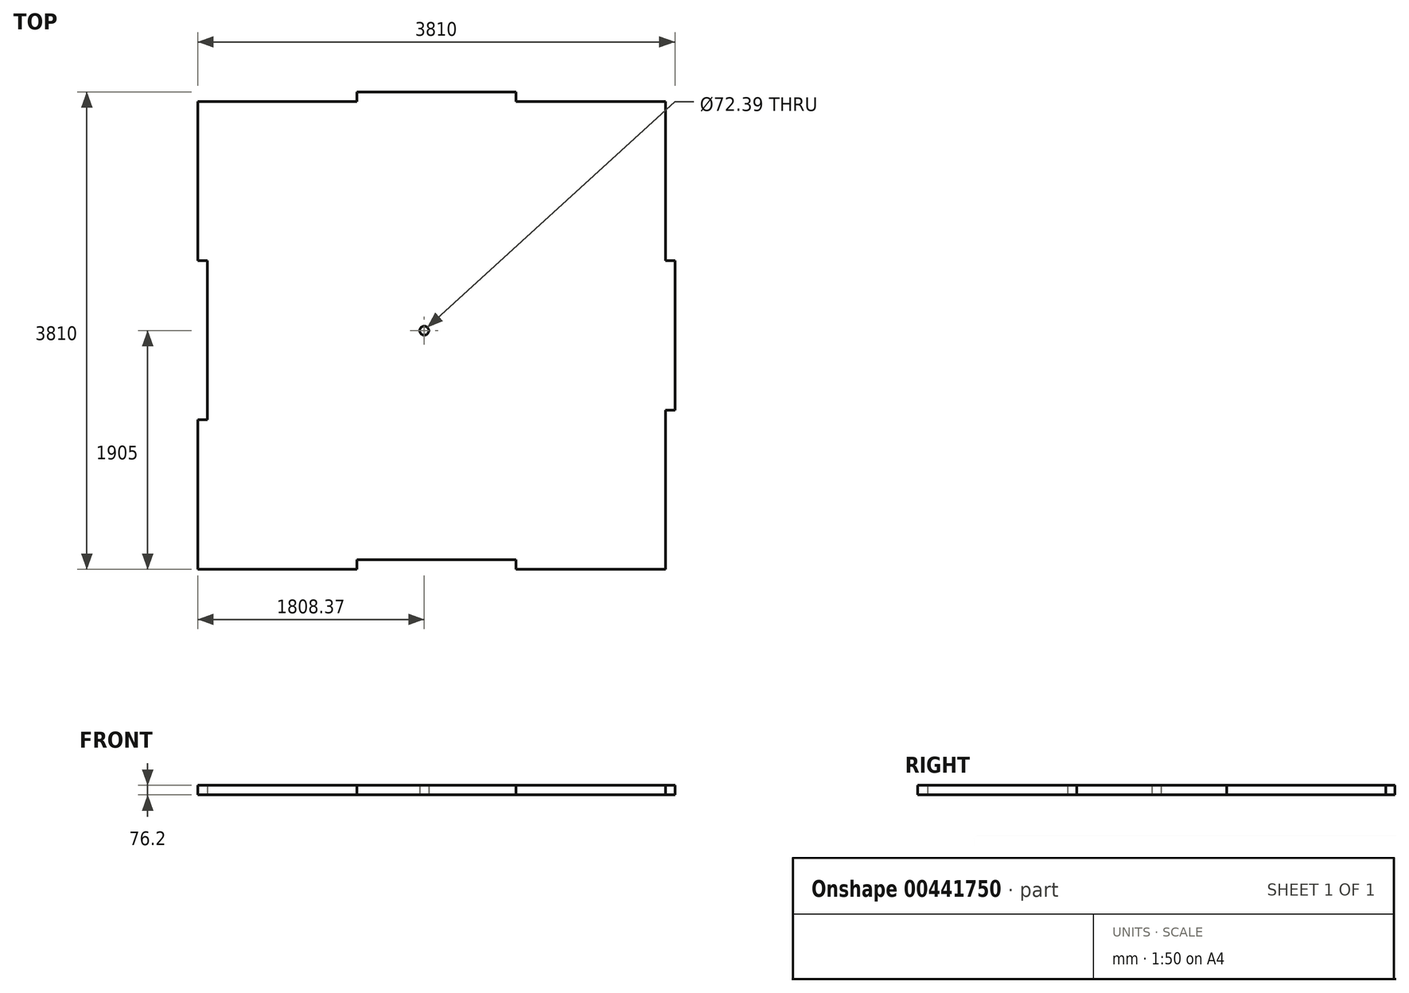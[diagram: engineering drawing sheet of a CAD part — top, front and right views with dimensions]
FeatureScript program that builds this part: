
annotation { "Feature Type Name" : "Feature", "Feature Type Description" : "" }
export const myFeature = defineFeature(function(context is Context, id is Id, definition is map)
    precondition{}
    {
        {
            var Q0;
            Q0=qCreatedBy(makeId("Top.planeOp"),FACE);
            var sketch = newSketch(context, id + "F0", { "sketchPlane" : qUnion([Q0])});
            skLineSegment(sketch, "E0.bottom", {"start": v(731.63, 1905) * mm, "end": v(-538.37, 1905) * mm});
            skLineSegment(sketch, "E0.top", {"start": v(1925.43, -1905) * mm, "end": v(731.63, -1905) * mm});
            skLineSegment(sketch, "E0.left", {"start": v(2001.63, 558.8) * mm, "end": v(2001.63, -635) * mm});
            skLineSegment(sketch, "E0.right", {"start": v(-1808.37, 1828.8) * mm, "end": v(-1808.37, 558.8) * mm});
            skPoint(sketch, "E0.middle", {"position": v(96.63, 0) * mm});
            skLineSegment(sketch, "E1", {"start": v(-1808.37, 1828.8) * mm, "end": v(-538.37, 1828.8) * mm});
            skLineSegment(sketch, "E2", {"start": v(-538.37, 1828.8) * mm, "end": v(-538.37, 1905) * mm});
            skLineSegment(sketch, "E3", {"start": v(1925.43, 1828.8) * mm, "end": v(731.63, 1828.8) * mm});
            skLineSegment(sketch, "E4", {"start": v(731.63, 1828.8) * mm, "end": v(731.63, 1905) * mm});
            skLineSegment(sketch, "E5", {"start": v(-1808.37, -1905) * mm, "end": v(-538.37, -1905) * mm});
            skLineSegment(sketch, "E6", {"start": v(-538.37, -1905) * mm, "end": v(-538.37, -1828.8) * mm});
            skLineSegment(sketch, "E7", {"start": v(-538.37, -1828.8) * mm, "end": v(731.63, -1828.8) * mm});
            skLineSegment(sketch, "E8", {"start": v(731.63, -1828.8) * mm, "end": v(731.63, -1905) * mm});
            skLineSegment(sketch, "E9.trimOffspring", {"start": v(-538.37, -1905) * mm, "end": v(-1808.37, -1905) * mm});
            skPoint(sketch, "E10.orphan", {"position": v(-1808.37, 1905) * mm});
            skPoint(sketch, "E11.orphan", {"position": v(2001.63, 1905) * mm});
            skLineSegment(sketch, "E12", {"start": v(-1808.37, 558.8) * mm, "end": v(-1732.17, 558.8) * mm});
            skLineSegment(sketch, "E13", {"start": v(-1732.17, 558.8) * mm, "end": v(-1732.17, -711.2) * mm});
            skLineSegment(sketch, "E14", {"start": v(-1732.17, -711.2) * mm, "end": v(-1808.37, -711.2) * mm});
            skLineSegment(sketch, "E15.trimOffspring", {"start": v(-1808.37, -711.2) * mm, "end": v(-1808.37, -1905) * mm});
            skLineSegment(sketch, "E16", {"start": v(1925.43, -1905) * mm, "end": v(1925.43, -635) * mm});
            skLineSegment(sketch, "E17", {"start": v(1925.43, -635) * mm, "end": v(2001.63, -635) * mm});
            skPoint(sketch, "E18.orphan", {"position": v(2001.63, -1905) * mm});
            skLineSegment(sketch, "E19", {"start": v(1925.43, 558.8) * mm, "end": v(2001.63, 558.8) * mm});
            skLineSegment(sketch, "E20", {"start": v(1925.43, 558.8) * mm, "end": v(1925.43, 1828.8) * mm});
            skCircle(sketch, "E21", {"center": v(0, 0) * mm, "radius": 36.2 * mm});
            skSolve(sketch);
        }
        {
            var Q0;
            Q0=makeQuery(id+"F0.imprint","IMPRINT",FACE,{"disambiguationData":[TD([[makeQuery(id+"F0.imprint","IMPRINT",EDGE,{"derivedFrom":sQuery(id+"F0.wireOp",EDGE,"E0.bottom")}),1.0]])]});
            extrude(context, id + "F1", {"entities" : qUnion([Q0]), "depth" : 76.2 * mm});
        }
    });
